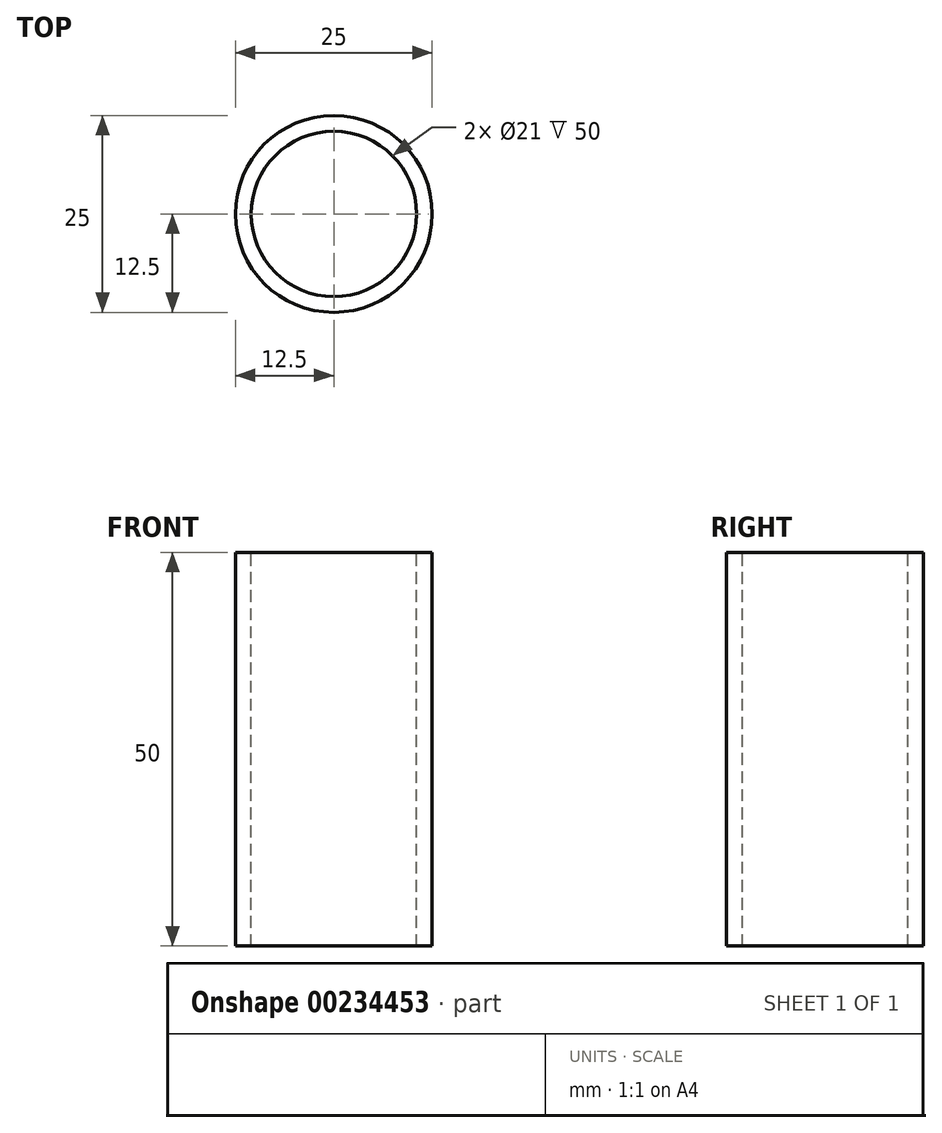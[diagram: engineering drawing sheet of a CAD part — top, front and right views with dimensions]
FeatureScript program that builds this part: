
annotation { "Feature Type Name" : "Feature", "Feature Type Description" : "" }
export const myFeature = defineFeature(function(context is Context, id is Id, definition is map)
    precondition{}
    {
        {
            var Q0;
            Q0=qCreatedBy(makeId("Front.planeOp"),FACE);
            var sketch = newSketch(context, id + "F0", { "sketchPlane" : qUnion([Q0])});
            skLineSegment(sketch, "E0.bottom", {"start": v(10.5, 50) * mm, "end": v(12.5, 50) * mm});
            skLineSegment(sketch, "E0.top", {"start": v(10.5, 0) * mm, "end": v(12.5, 0) * mm});
            skLineSegment(sketch, "E0.left", {"start": v(10.5, 50) * mm, "end": v(10.5, 0) * mm});
            skLineSegment(sketch, "E0.right", {"start": v(12.5, 50) * mm, "end": v(12.5, 0) * mm});
            skLineSegment(sketch, "E1", {"start": v(0, 61.9) * mm, "end": v(0, -6.18) * mm, "construction": true});
            skSolve(sketch);
        }
        {
            var Q0;
            Q0=makeQuery(id+"F0.imprint","IMPRINT",FACE,{"disambiguationData":[TD([[makeQuery(id+"F0.imprint","IMPRINT",EDGE,{"derivedFrom":sQuery(id+"F0.wireOp",EDGE,"E0.bottom")}),-1.0]])]});
            var Q1;
            Q1=sQuery(id+"F0.wireOp",EDGE,"E1");
            revolve(context, id + "F1", {"entities" : qUnion([Q0]), "axis" : qUnion([Q1]), "revolveType" : RevolveType.FULL});
        }
    });
